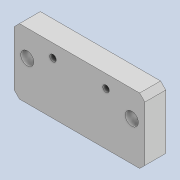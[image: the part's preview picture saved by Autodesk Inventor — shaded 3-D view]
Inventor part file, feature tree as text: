
AUTODESK INVENTOR PART (.ipt)
format: ipt  version: 2020 (Build 240168000, 168)  size: 110,592 bytes
history: native  units: mm
features: extrude x1, chamfer x1, sketch x1
ambient origin geometry x8: Origin, YZ Plane, XZ Plane, XY Plane, X Axis, Y Axis, Z Axis, Center Point
bodies: Solid1 (feature_tree)
feature tree (3):
  extrude  "Extrusion1"  Depth=50.0mm
  chamfer  "Chamfer1"  Distance=35.0mm
  sketch  "Sketch1"  dims[d0=25.0mm d1=50.0mm d2=35.0mm d3=20.0mm d4=5.0mm d5=5.0mm d6=5.0mm d7=10.0mm d8=2.5mm d9=2.5mm d10=5.0mm d11=20.3mm d12=8.0mm d13=0.0mm d14=2.0mm d15=2.0mm d16=45.0deg]
